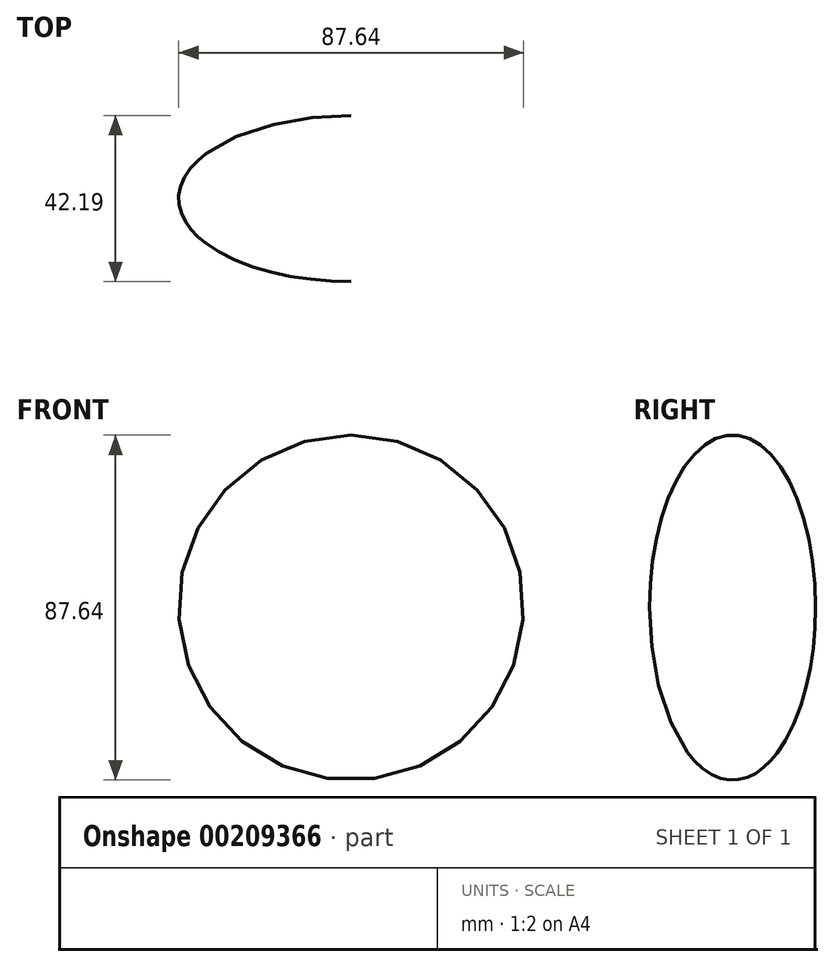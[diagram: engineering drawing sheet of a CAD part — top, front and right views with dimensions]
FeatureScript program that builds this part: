
annotation { "Feature Type Name" : "Feature", "Feature Type Description" : "" }
export const myFeature = defineFeature(function(context is Context, id is Id, definition is map)
    precondition{}
    {
        {
            var Q0;
            Q0=qCreatedBy(makeId("Right.planeOp"),FACE);
            var sketch = newSketch(context, id + "F0", { "sketchPlane" : qUnion([Q0])});
            skLineSegment(sketch, "E0.bottom", {"start": v(37.52, -35.61) * mm, "end": v(24.54, -35.61) * mm});
            skLineSegment(sketch, "E0.top", {"start": v(37.52, 35.61) * mm, "end": v(24.54, 35.61) * mm});
            skLineSegment(sketch, "E0.left", {"start": v(37.52, 24.55) * mm, "end": v(37.52, 35.61) * mm});
            skLineSegment(sketch, "E0.right", {"start": v(24.54, -35.61) * mm, "end": v(24.54, 35.61) * mm});
            skPoint(sketch, "E0.middle", {"position": v(31.03, 0) * mm});
            skLineSegment(sketch, "E1.bottom", {"start": v(9.94, 19.55) * mm, "end": v(32.52, 19.55) * mm});
            skLineSegment(sketch, "E1.top", {"start": v(9.94, 10.43) * mm, "end": v(53.54, 10.43) * mm});
            skLineSegment(sketch, "E1.left", {"start": v(9.94, 19.55) * mm, "end": v(9.94, 10.43) * mm});
            skLineSegment(sketch, "E1.right", {"start": v(53.54, 19.55) * mm, "end": v(53.54, 10.43) * mm});
            skArc(sketch, "E2.filletArc", {"start": v(32.52, 19.55) * mm, "mid": v(36.06, 21.02) * mm, "end": v(37.52, 24.55) * mm});
            skSolve(sketch);
        }
        {
            var Q0;
            {var subQ1=sQuery(id+"F0.wireOp",EDGE,"E0.top");Q0=makeQuery(id+"F0.imprint","IMPRINT",FACE,{"disambiguationData":[TD([[makeQuery(id+"F0.imprint","IMPRINT",EDGE,{"derivedFrom":subQ1}),1.0]])]});}
            var Q1;
            {var subQ5=sQuery(id+"F0.wireOp",EDGE,"E1.left");Q1=makeQuery(id+"F0.imprint","IMPRINT",FACE,{"disambiguationData":[TD([[makeQuery(id+"F0.imprint","IMPRINT",EDGE,{"derivedFrom":subQ5}),1.0]])]});}
            extrude(context, id + "F1", {"entities" : qUnion([Q0, Q1]), "depth" : 0.04 * yard});
        }
        {
            var Q0;
            Q0=makeQuery(id+"F1.opExtrude","SWEPT_BODY",BODY,{"disambiguationData":[OSD([sQuery(id+"F0.wireOp",EDGE,"E0.right"),sQuery(id+"F0.wireOp",EDGE,"E1.bottom"),sQuery(id+"F0.wireOp",EDGE,"E1.top"),sQuery(id+"F0.wireOp",EDGE,"E1.left")])]});
            deleteBodies(context, id + "F2", {"entities" : qUnion([Q0])});
        }
        {
            var Q0;
            Q0=makeQuery(id+"F1.opExtrude","SWEPT_BODY",BODY,{"disambiguationData":[OSD([sQuery(id+"F0.wireOp",EDGE,"E0.top"),sQuery(id+"F0.wireOp",EDGE,"E0.left"),sQuery(id+"F0.wireOp",EDGE,"E0.right"),sQuery(id+"F0.wireOp",EDGE,"E1.bottom"),sQuery(id+"F0.wireOp",EDGE,"E2.filletArc")])]});
            deleteBodies(context, id + "F3", {"entities" : qUnion([Q0])});
        }
        {
            var Q0;
            Q0=qCreatedBy(makeId("Right.planeOp"),FACE);
            var sketch = newSketch(context, id + "F4", { "sketchPlane" : qUnion([Q0])});
            skLineSegment(sketch, "E3.right", {"start": v(-12.73, -27.81) * mm, "end": v(-12.73, 27.81) * mm});
            skPoint(sketch, "E3.middle", {"position": v(0, 0) * mm});
            skArc(sketch, "E4", {"start": v(12.73, 27.81) * mm, "mid": v(0, 40.54) * mm, "end": v(-12.73, 27.81) * mm});
            skArc(sketch, "E5", {"start": v(-12.73, -27.81) * mm, "mid": v(0, -40.54) * mm, "end": v(12.73, -27.81) * mm});
            skLineSegment(sketch, "E6.left", {"start": v(6.7, -27.81) * mm, "end": v(6.7, 27.81) * mm});
            skLineSegment(sketch, "E6.right", {"start": v(-6.7, -27.81) * mm, "end": v(-6.7, 27.81) * mm});
            skArc(sketch, "E7", {"start": v(-6.7, -27.81) * mm, "mid": v(0, -34.52) * mm, "end": v(6.7, -27.81) * mm});
            skArc(sketch, "E8", {"start": v(6.7, 27.81) * mm, "mid": v(0, 34.52) * mm, "end": v(-6.7, 27.81) * mm});
            skLineSegment(sketch, "E9", {"start": v(12.73, 27.81) * mm, "end": v(12.73, -27.81) * mm});
            skCircle(sketch, "E10", {"center": v(-9.97, 23.8) * mm, "radius": 1.98 * mm});
            skCircle(sketch, "E11", {"center": v(-9.7, 16.92) * mm, "radius": 2.1 * mm});
            skCircle(sketch, "E12", {"center": v(-10.1, 11.02) * mm, "radius": 2.2 * mm});
            skCircle(sketch, "E13", {"center": v(-10.12, 4.67) * mm, "radius": 1.77 * mm});
            skSolve(sketch);
        }
        {
            var Q0;
            Q0 = qSketchRegion(id + "F4", true);
            extrude(context, id + "F5", {"entities" : qUnion([Q0]), "depth" : 0 * yard});
        }
        {
            var Q0;
            Q0=makeQuery(id+"F5.opExtrude","SWEPT_BODY",BODY,{"disambiguationData":[OSD([sQuery(id+"F4.wireOp",EDGE,"E3.right"),sQuery(id+"F4.wireOp",EDGE,"E4"),sQuery(id+"F4.wireOp",EDGE,"E5"),sQuery(id+"F4.wireOp",EDGE,"E6.left"),sQuery(id+"F4.wireOp",EDGE,"E6.right"),sQuery(id+"F4.wireOp",EDGE,"E7"),sQuery(id+"F4.wireOp",EDGE,"E8"),sQuery(id+"F4.wireOp",EDGE,"E9"),sQuery(id+"F4.wireOp",EDGE,"E10"),sQuery(id+"F4.wireOp",EDGE,"E11"),sQuery(id+"F4.wireOp",EDGE,"E12"),sQuery(id+"F4.wireOp",EDGE,"E13")])]});
            deleteBodies(context, id + "F6", {"entities" : qUnion([Q0])});
        }
        {
            var Q0;
            Q0=qCreatedBy(makeId("Right.planeOp"),FACE);
            var sketch = newSketch(context, id + "F7", { "sketchPlane" : qUnion([Q0])});
            skEllipticalArc(sketch, "E14", {});
            skLineSegment(sketch, "E15", {"start": v(0, 50.93) * mm, "end": v(0, 0) * mm});
            skLineSegment(sketch, "E16", {"start": v(0, 0) * mm, "end": v(68.83, 0) * mm});
            const initialGuessF7  = {"E14": [0.029742872342467308, 0, 0, -1, 0.043820321559906006, 0.02109492791375058, 1.5707963267948966, 4.71238898038469]};
            skSetInitialGuess(sketch, initialGuessF7);
            skSolve(sketch);
        }
        {
            var Q0;
            {var subQ0=sQuery(id+"F7.wireOp",EDGE,"E14");Q0=makeQuery(id+"F7.imprint","IMPRINT",FACE,{"disambiguationData":[TD([[makeQuery(id+"F7.imprint","IMPRINT",EDGE,{"derivedFrom":subQ0}),1.0]])]});}
            var Q1;
            Q1=sQuery(id+"F7.wireOp",EDGE,"E16");
            revolve(context, id + "F8", {"entities" : qUnion([Q0]), "axis" : qUnion([Q1]), "revolveType" : RevolveType.FULL});
        }
    });
